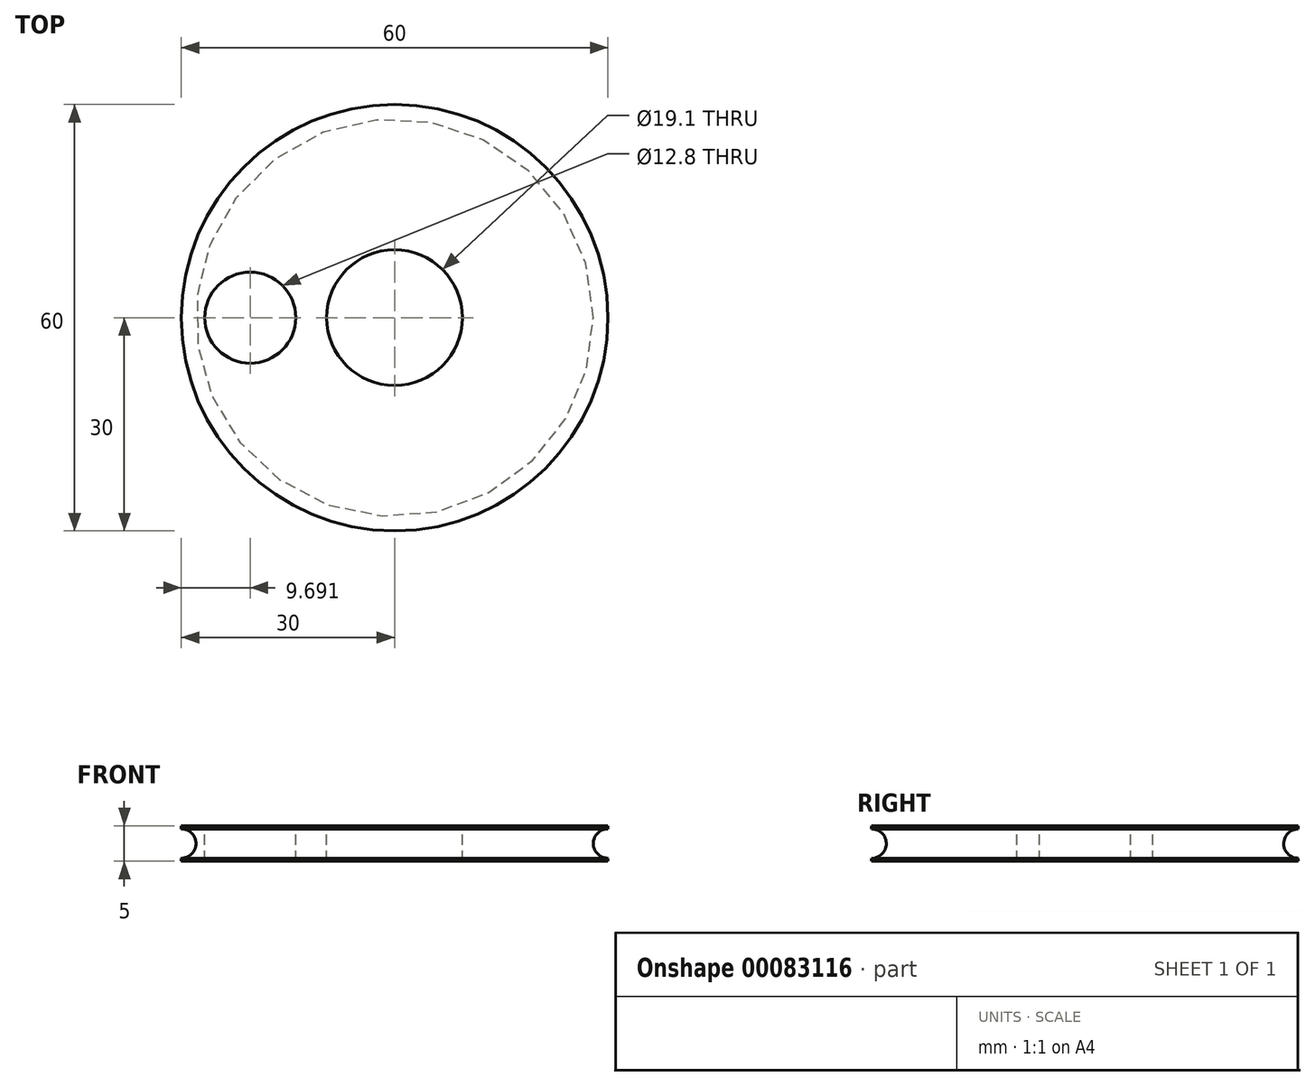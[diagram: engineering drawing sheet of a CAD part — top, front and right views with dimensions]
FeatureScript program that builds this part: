
annotation { "Feature Type Name" : "Feature", "Feature Type Description" : "" }
export const myFeature = defineFeature(function(context is Context, id is Id, definition is map)
    precondition{}
    {
        {
            var Q0;
            Q0=qCreatedBy(makeId("Top.planeOp"),FACE);
            var sketch = newSketch(context, id + "F0", { "sketchPlane" : qUnion([Q0])});
            skCircle(sketch, "E0", {"center": v(0, 0) * mm, "radius": 30 * mm});
            skSolve(sketch);
        }
        {
            var Q0;
            Q0=makeQuery(id+"F0.imprint","IMPRINT",FACE,{"disambiguationData":[TD([[makeQuery(id+"F0.imprint","IMPRINT",EDGE,{"derivedFrom":sQuery(id+"F0.wireOp",EDGE,"E0")}),1.0]])]});
            extrude(context, id + "F1", {"entities" : qUnion([Q0]), "depth" : 5 * mm});
        }
        {
            var Q0;
            Q0=makeQuery(id+"F1.opExtrude","CAP_FACE",FACE,{"disambiguationData":[OSD([sQuery(id+"F0.wireOp",EDGE,"E0")])],"isStart":false});
            var sketch = newSketch(context, id + "F2", { "sketchPlane" : qUnion([Q0])});
            skCircle(sketch, "E1", {"center": v(0, 0) * mm, "radius": 9.55 * mm});
            skSolve(sketch);
        }
        {
            var Q0;
            Q0 = qSketchRegion(id + "F2", true);
            extrude(context, id + "F3", {"entities" : qUnion([Q0]), "operationType" : NewBodyOperationType.REMOVE, "oppositeDirection" : true, "depth" : 5.5 * mm});
        }
        {
            var Q0;
            Q0=qCreatedBy(makeId("Right.planeOp"),FACE);
            var sketch = newSketch(context, id + "F4", { "sketchPlane" : qUnion([Q0])});
            skCircle(sketch, "E2", {"center": v(30, 2.5) * mm, "radius": 2.06 * mm});
            skSolve(sketch);
        }
        {
            var Q0;
            Q0=makeQuery(id+"F4.imprint","IMPRINT",FACE,{"disambiguationData":[TD([[makeQuery(id+"F4.imprint","IMPRINT",EDGE,{"derivedFrom":sQuery(id+"F4.wireOp",EDGE,"E2")}),1.0]])]});
            var Q1;
            Q1 = qConstructionFilter(qBodyType(qCreatedBy(id + "F0" ,EDGE), BodyType.WIRE), ConstructionObject.NO);
            sweep(context, id + "F5", {"operationType" : NewBodyOperationType.REMOVE, "profiles" : qUnion([Q0]), "path" : qUnion([Q1])});
        }
        {
            var Q0;
            Q0=makeQuery(id+"F1.opExtrude","CAP_FACE",FACE,{"disambiguationData":[OSD([sQuery(id+"F0.wireOp",EDGE,"E0")])],"isStart":false});
            var sketch = newSketch(context, id + "F6", { "sketchPlane" : qUnion([Q0])});
            skCircle(sketch, "E3", {"center": v(-20.3, 0) * mm, "radius": 6.4 * mm});
            skSolve(sketch);
        }
        {
            var Q0;
            Q0=makeQuery(id+"F6.imprint","IMPRINT",FACE,{"disambiguationData":[TD([[makeQuery(id+"F6.imprint","IMPRINT",EDGE,{"derivedFrom":sQuery(id+"F6.wireOp",EDGE,"E3")}),1.0]])]});
            extrude(context, id + "F7", {"entities" : qUnion([Q0]), "operationType" : NewBodyOperationType.REMOVE, "oppositeDirection" : true, "depth" : 5.1 * mm});
        }
    });
